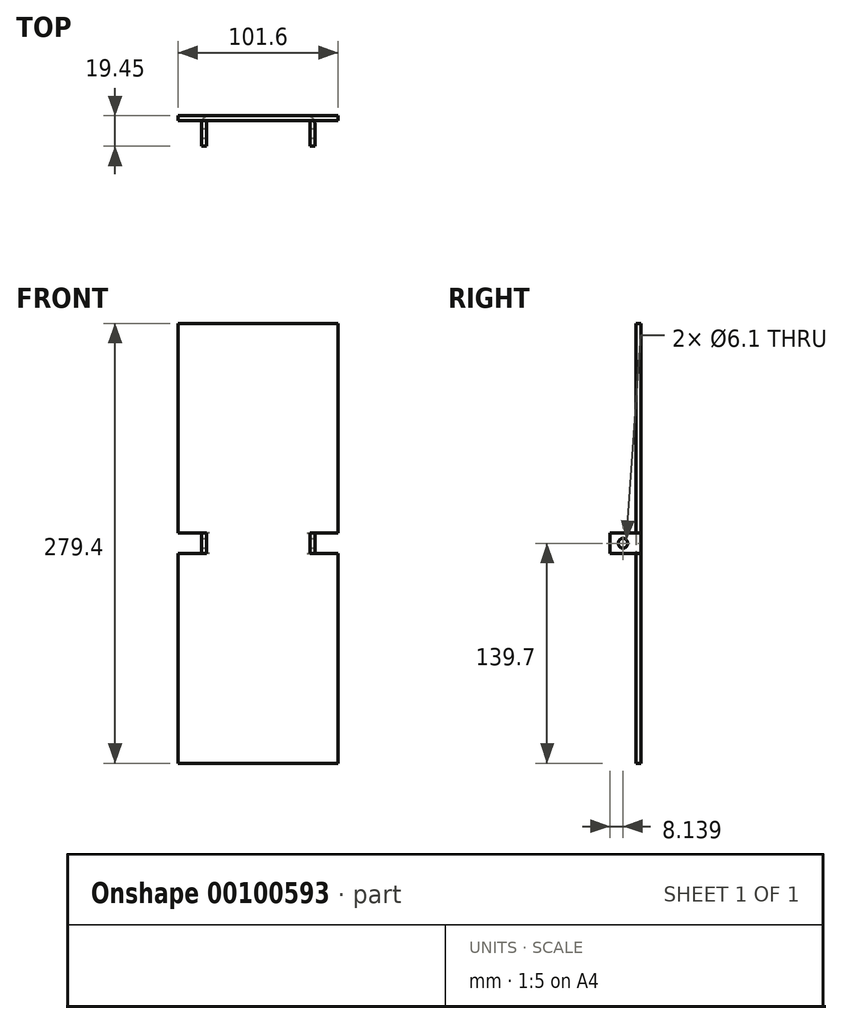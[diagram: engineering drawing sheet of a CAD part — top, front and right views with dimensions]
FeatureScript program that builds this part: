
annotation { "Feature Type Name" : "Feature", "Feature Type Description" : "" }
export const myFeature = defineFeature(function(context is Context, id is Id, definition is map)
    precondition{}
    {
        {
            var Q0;
            Q0=qCreatedBy(makeId("Front.planeOp"),FACE);
            var sketch = newSketch(context, id + "F0", { "sketchPlane" : qUnion([Q0])});
            skLineSegment(sketch, "E0.bottom", {"start": v(-50.8, 139.7) * mm, "end": v(50.8, 139.7) * mm});
            skLineSegment(sketch, "E0.top", {"start": v(-50.8, -139.7) * mm, "end": v(50.8, -139.7) * mm});
            skLineSegment(sketch, "E0.left", {"start": v(-50.8, 139.7) * mm, "end": v(-50.8, -139.7) * mm});
            skLineSegment(sketch, "E0.right", {"start": v(50.8, 139.7) * mm, "end": v(50.8, -139.7) * mm});
            skPoint(sketch, "E0.middle", {"position": v(0, 0) * mm});
            skSolve(sketch);
        }
        {
            var Q0;
            Q0=makeQuery(id+"F0.imprint","IMPRINT",FACE,{"disambiguationData":[TD([[makeQuery(id+"F0.imprint","IMPRINT",EDGE,{"derivedFrom":sQuery(id+"F0.wireOp",EDGE,"E0.bottom")}),-1.0]])]});
            extrude(context, id + "F1", {"entities" : qUnion([Q0]), "depth" : 3.17 * mm});
        }
        {
            var Q0;
            Q0=makeQuery(id+"F1.opExtrude","CAP_FACE",FACE,{"disambiguationData":[OSD([sQuery(id+"F0.wireOp",EDGE,"E0.bottom"),sQuery(id+"F0.wireOp",EDGE,"E0.top"),sQuery(id+"F0.wireOp",EDGE,"E0.left"),sQuery(id+"F0.wireOp",EDGE,"E0.right")])],"isStart":false});
            var sketch = newSketch(context, id + "F2", { "sketchPlane" : qUnion([Q0])});
            skLineSegment(sketch, "E1.bottom", {"start": v(32.85, 6.5) * mm, "end": v(36.03, 6.5) * mm});
            skLineSegment(sketch, "E1.top", {"start": v(32.85, -6.5) * mm, "end": v(36.03, -6.5) * mm});
            skLineSegment(sketch, "E1.left", {"start": v(32.85, 6.5) * mm, "end": v(32.85, -6.5) * mm});
            skLineSegment(sketch, "E1.right", {"start": v(36.03, 6.5) * mm, "end": v(36.03, -6.5) * mm});
            skLineSegment(sketch, "E2.bottom", {"start": v(36.03, 6.5) * mm, "end": v(50.8, 6.5) * mm});
            skLineSegment(sketch, "E2.top", {"start": v(36.03, -6.5) * mm, "end": v(50.8, -6.5) * mm});
            skLineSegment(sketch, "E2.right", {"start": v(50.8, 6.5) * mm, "end": v(50.8, -6.5) * mm});
            skLineSegment(sketch, "E3.MirrorCS", {"start": v(-32.85, 6.5) * mm, "end": v(-36.03, 6.5) * mm});
            skLineSegment(sketch, "E4.MirrorCS", {"start": v(-32.85, 6.5) * mm, "end": v(-32.85, -6.5) * mm});
            skLineSegment(sketch, "E5.MirrorCS", {"start": v(-32.85, -6.5) * mm, "end": v(-36.03, -6.5) * mm});
            skLineSegment(sketch, "E6.MirrorCS", {"start": v(-36.03, 6.5) * mm, "end": v(-36.03, -6.5) * mm});
            skLineSegment(sketch, "E7.MirrorCS", {"start": v(-36.03, -6.5) * mm, "end": v(-50.8, -6.5) * mm});
            skLineSegment(sketch, "E8.MirrorCS", {"start": v(-50.8, 6.5) * mm, "end": v(-50.8, -6.5) * mm});
            skLineSegment(sketch, "E9.MirrorCS", {"start": v(-36.03, 6.5) * mm, "end": v(-50.8, 6.5) * mm});
            skSolve(sketch);
        }
        {
            var Q0;
            Q0=makeQuery(id+"F2.imprint","IMPRINT",FACE,{"disambiguationData":[TD([[makeQuery(id+"F2.imprint","IMPRINT",EDGE,{"derivedFrom":sQuery(id+"F2.wireOp",EDGE,"E1.bottom")}),-1.0]])]});
            var Q1;
            Q1=makeQuery(id+"F2.imprint","IMPRINT",FACE,{"disambiguationData":[TD([[makeQuery(id+"F2.imprint","IMPRINT",EDGE,{"derivedFrom":sQuery(id+"F2.wireOp",EDGE,"E3.MirrorCS")}),1.0]])]});
            extrude(context, id + "F3", {"entities" : qUnion([Q0, Q1]), "operationType" : NewBodyOperationType.ADD, "depth" : 16.27 * mm});
        }
        {
            var Q0;
            Q0=makeQuery(id+"F2.imprint","IMPRINT",FACE,{"disambiguationData":[TD([[makeQuery(id+"F2.imprint","IMPRINT",EDGE,{"derivedFrom":sQuery(id+"F2.wireOp",EDGE,"E2.bottom")}),-1.0]])]});
            var Q1;
            Q1=makeQuery(id+"F2.imprint","IMPRINT",FACE,{"disambiguationData":[TD([[makeQuery(id+"F2.imprint","IMPRINT",EDGE,{"derivedFrom":sQuery(id+"F2.wireOp",EDGE,"E6.MirrorCS")}),-1.0]])]});
            extrude(context, id + "F4", {"entities" : qUnion([Q0, Q1]), "operationType" : NewBodyOperationType.REMOVE, "oppositeDirection" : true, "depth" : 25.4 * mm});
        }
        {
            var Q0;
            Q0=makeQuery(id+"F4.boolean.opBoolean","INTERSECT",EDGE,{"derivedFrom":[makeQuery(id+"F1.opExtrude","CAP_FACE",FACE,{"disambiguationData":[OSD([sQuery(id+"F0.wireOp",EDGE,"E0.bottom"),sQuery(id+"F0.wireOp",EDGE,"E0.top"),sQuery(id+"F0.wireOp",EDGE,"E0.left"),sQuery(id+"F0.wireOp",EDGE,"E0.right")])],"isStart":true}),makeQuery(id+"F4.opExtrude","SWEPT_FACE",FACE,{"disambiguationData":[OSD([sQuery(id+"F2.wireOp",EDGE,"E1.right")])]})]});
            var Q1;
            Q1=makeQuery(id+"F4.boolean.opBoolean","INTERSECT",EDGE,{"derivedFrom":[makeQuery(id+"F1.opExtrude","CAP_FACE",FACE,{"disambiguationData":[OSD([sQuery(id+"F0.wireOp",EDGE,"E0.bottom"),sQuery(id+"F0.wireOp",EDGE,"E0.top"),sQuery(id+"F0.wireOp",EDGE,"E0.left"),sQuery(id+"F0.wireOp",EDGE,"E0.right")])],"isStart":true}),makeQuery(id+"F4.opExtrude","SWEPT_FACE",FACE,{"disambiguationData":[OSD([sQuery(id+"F2.wireOp",EDGE,"E6.MirrorCS")])]})]});
            fillet(context, id + "F5", {"entities" : qUnion([Q0, Q1]), "radius" : 5.08 * mm, "tangentPropagation" : true, "allowEdgeOverflow" : false});
        }
        {
            var Q0;
            {var subQ0=sQuery(id+"F2.wireOp",EDGE,"E1.right");Q0=makeQuery(id+"F4.boolean.opBoolean","MERGE",FACE,{"derivedFrom":[makeQuery(id+"F3.opExtrude","SWEPT_FACE",FACE,{"disambiguationData":[OSD([subQ0])]}),makeQuery(id+"F4.opExtrude","SWEPT_FACE",FACE,{"disambiguationData":[OSD([subQ0])]})]});}
            var sketch = newSketch(context, id + "F6", { "sketchPlane" : qUnion([Q0])});
            skPoint(sketch, "E10", {"position": v(-11.31, 0) * mm});
            skSolve(sketch);
        }
        {
            var Q0;
            Q0=sQuery(id+"F6.wireOp",VERTEX,"E10");
            var Q1;
            Q1=makeQuery(id+"F1.opExtrude","SWEPT_BODY",BODY,{"disambiguationData":[OSD([sQuery(id+"F0.wireOp",EDGE,"E0.bottom"),sQuery(id+"F0.wireOp",EDGE,"E0.top"),sQuery(id+"F0.wireOp",EDGE,"E0.left"),sQuery(id+"F0.wireOp",EDGE,"E0.right")])]});
            hole(context, id + "F7", {"style" : HoleStyle.SIMPLE, "endStyle" : HoleEndStyle.THROUGH, "holeDiameter" : 6.1 * mm, "locations" : qUnion([Q0]), "scope" : qUnion([Q1]), "isTappedThrough" : true});
        }
    });
